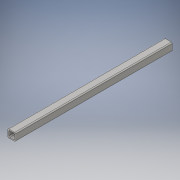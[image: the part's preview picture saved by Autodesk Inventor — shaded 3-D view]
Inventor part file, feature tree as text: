
AUTODESK INVENTOR PART (.ipt)
format: ipt  version: 2016 (Build 200138000, 138)  size: 114,176 bytes
history: native  units: in
note: dims shown in document units (in); Inventor stores cm internally (conversion verified against a paired STEP export)
features: extrude x1, sketch x1
ambient origin geometry x8: Origin, YZ Plane, XZ Plane, XY Plane, X Axis, Y Axis, Z Axis, Center Point
bodies: Solid1 (feature_tree)
feature tree (2):
  extrude  "Extrusion1"  Depth=1.0in
  sketch  "Sketch1"  dims[d0=1.0in d1=1.0in d2=0.125in d3=0.125in d4=20.0in d5=0.0in]
